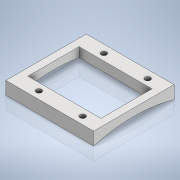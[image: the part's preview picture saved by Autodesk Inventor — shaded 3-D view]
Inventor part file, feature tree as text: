
AUTODESK INVENTOR PART (.ipt)
format: ipt  version: 2022 (Build 260153000, 153)  size: 161,792 bytes
history: native  units: mm
features: extrude x3, sketch x3, other x3, reference x1
ambient origin geometry x8: Origin, YZ Plane, XZ Plane, XY Plane, X Axis, Y Axis, Z Axis, Center Point
bodies: Solid1 (feature_tree)
feature tree (10):
  extrude  "Extrusion1"  Depth=11.0mm
  extrude  "Extrusion2"  Depth=7.5mm
  extrude  "Extrusion3"  Depth=7.0mm
  sketch  "Sketch1"  dims[d0=12.0mm d1=11.0mm]
  sketch  "Sketch2"  dims[d2=5.5mm d3=7.5mm]
  reference  "Reference1"
  sketch  "Sketch3"  dims[d4=10.0mm d5=7.0mm d6=2.0mm d7=1.0mm d8=0.75mm d9=3.5mm d10=1.0mm d11=20.0mm d13=8.9mm d14=20.0mm d16=6.0mm d19=1.0mm d20=0.0mm d21=10.0mm d22=0.0mm d23=0.0mm d24=0.0mm]
  other  "<userpath>\Documents\Telescope\Telescope.iam"
  other  "Telescope.iam"
  other  "Aperture:1"
